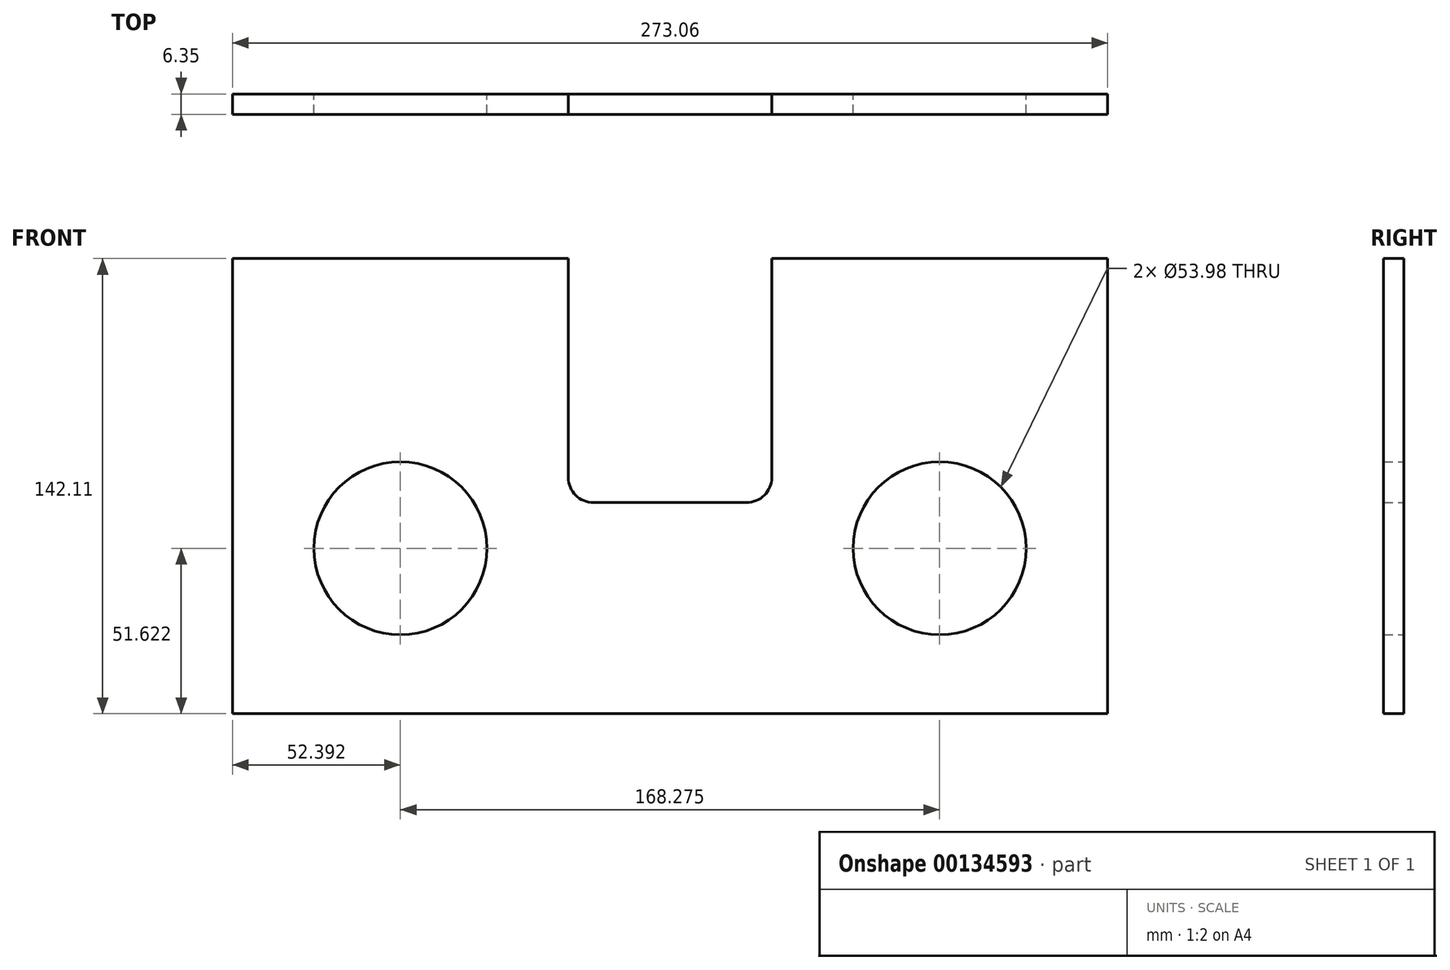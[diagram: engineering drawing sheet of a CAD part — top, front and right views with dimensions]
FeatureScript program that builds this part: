
annotation { "Feature Type Name" : "Feature", "Feature Type Description" : "" }
export const myFeature = defineFeature(function(context is Context, id is Id, definition is map)
    precondition{}
    {
        {
            var Q0;
            Q0=qCreatedBy(makeId("Front.planeOp"),FACE);
            var sketch = newSketch(context, id + "F0", { "sketchPlane" : qUnion([Q0])});
            skLineSegment(sketch, "E0.bottom", {"start": v(-136.53, 76.2) * mm, "end": v(-31.75, 76.2) * mm});
            skLineSegment(sketch, "E0.top", {"start": v(-136.52, -65.91) * mm, "end": v(136.53, -65.91) * mm});
            skLineSegment(sketch, "E0.left", {"start": v(-136.52, 76.2) * mm, "end": v(-136.52, -65.91) * mm});
            skLineSegment(sketch, "E0.right", {"start": v(136.53, 76.2) * mm, "end": v(136.53, -65.91) * mm});
            skCircle(sketch, "E1", {"center": v(-84.14, -14.29) * mm, "radius": 26.99 * mm});
            skCircle(sketch, "E2", {"center": v(84.14, -14.29) * mm, "radius": 26.99 * mm});
            skLineSegment(sketch, "E3", {"start": v(31.75, 76.2) * mm, "end": v(31.75, 7.87) * mm});
            skLineSegment(sketch, "E4", {"start": v(23.88, 0) * mm, "end": v(-23.88, 0) * mm});
            skLineSegment(sketch, "E5", {"start": v(-31.75, 7.87) * mm, "end": v(-31.75, 76.2) * mm});
            skPoint(sketch, "E6", {"position": v(0, 0) * mm});
            skLineSegment(sketch, "E7.trimOffspring", {"start": v(31.75, 76.2) * mm, "end": v(136.53, 76.2) * mm});
            skPoint(sketch, "E8.visualSharp", {"position": v(-31.75, 0) * mm});
            skArc(sketch, "E8.filletArc", {"start": v(-31.75, 7.87) * mm, "mid": v(-29.44, 2.3) * mm, "end": v(-23.88, 0) * mm});
            skPoint(sketch, "E9.visualSharp", {"position": v(31.75, 0) * mm});
            skArc(sketch, "E9.filletArc", {"start": v(23.88, 0) * mm, "mid": v(29.44, 2.3) * mm, "end": v(31.75, 7.87) * mm});
            skPoint(sketch, "E10", {"position": v(0, -65.91) * mm});
            skSolve(sketch);
        }
        {
            var Q0;
            Q0 = qSketchRegion(id + "F0", true);
            extrude(context, id + "F1", {"entities" : qUnion([Q0]), "depth" : 6.35 * mm});
        }
    });
